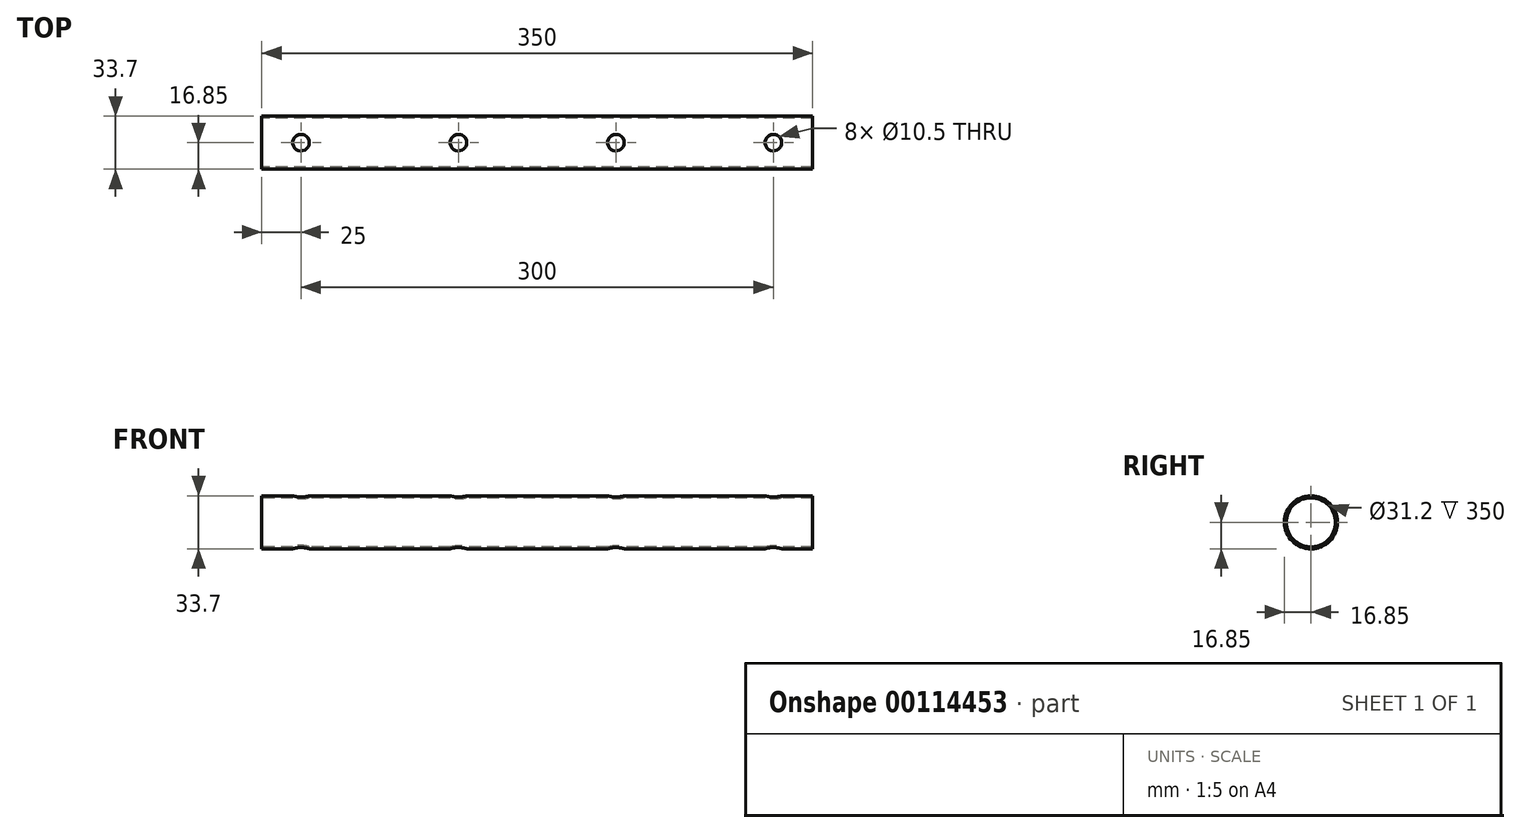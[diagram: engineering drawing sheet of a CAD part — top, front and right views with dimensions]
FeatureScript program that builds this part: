
annotation { "Feature Type Name" : "Feature", "Feature Type Description" : "" }
export const myFeature = defineFeature(function(context is Context, id is Id, definition is map)
    precondition{}
    {
        {
            var Q0;
            Q0=qCreatedBy(makeId("Right.planeOp"),FACE);
            var sketch = newSketch(context, id + "F0", { "sketchPlane" : qUnion([Q0])});
            skCircle(sketch, "E0", {"center": v(0, 0) * mm, "radius": 16.85 * mm});
            skCircle(sketch, "E1", {"center": v(0, 0) * mm, "radius": 15.6 * mm});
            skSolve(sketch);
        }
        {
            var Q0;
            Q0 = qSketchRegion(id + "F0", true);
            extrude(context, id + "F1", {"entities" : qUnion([Q0]), "depth" : 350 * mm});
        }
        {
            var Q0;
            Q0=qCreatedBy(makeId("Top.planeOp"),FACE);
            cPlane(context, id + "F2", {"entities" : qUnion([Q0]), "cplaneType" : CPlaneType.OFFSET, "offset" : 17 * mm, "width" : 150 * mm, "height" : 150 * mm});
        }
        {
            var Q0;
            Q0=qCreatedBy(id+"F2.planeOp",FACE);
            var sketch = newSketch(context, id + "F3", { "sketchPlane" : qUnion([Q0])});
            skCircle(sketch, "E2", {"center": v(25, 0) * mm, "radius": 5.25 * mm});
            skCircle(sketch, "E3", {"center": v(125, 0) * mm, "radius": 5.25 * mm});
            skCircle(sketch, "E4", {"center": v(325, 0) * mm, "radius": 5.25 * mm});
            skCircle(sketch, "E5", {"center": v(225, 0) * mm, "radius": 5.25 * mm});
            skSolve(sketch);
        }
        {
            var Q0;
            Q0 = qSketchRegion(id + "F3", true);
            extrude(context, id + "F4", {"entities" : qUnion([Q0]), "operationType" : NewBodyOperationType.REMOVE, "endBound" : BoundingType.THROUGH_ALL, "oppositeDirection" : true, "depth" : 25 * mm});
        }
    });
